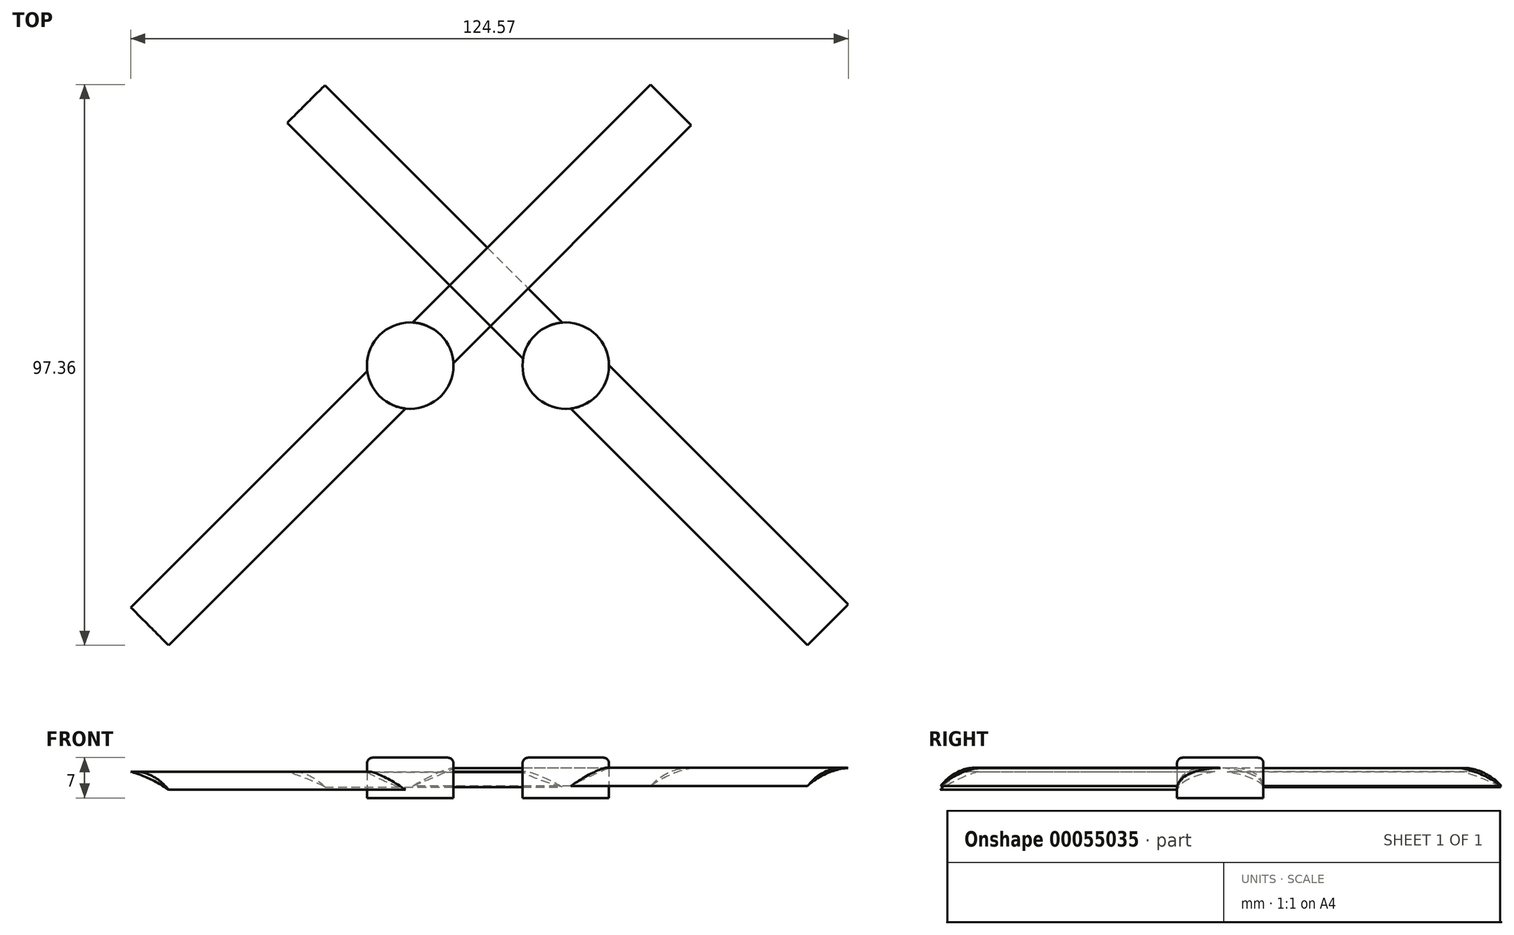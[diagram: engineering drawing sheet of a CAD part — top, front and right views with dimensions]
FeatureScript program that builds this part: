
annotation { "Feature Type Name" : "Feature", "Feature Type Description" : "" }
export const myFeature = defineFeature(function(context is Context, id is Id, definition is map)
    precondition{}
    {
        {
            var Q0;
            Q0=qCreatedBy(makeId("Top.planeOp"),FACE);
            var sketch = newSketch(context, id + "F0", { "sketchPlane" : qUnion([Q0])});
            skCircle(sketch, "E0", {"center": v(0, 0) * mm, "radius": 7.5 * mm});
            skCircle(sketch, "E1", {"center": v(27, 0) * mm, "radius": 7.5 * mm});
            skSolve(sketch);
        }
        {
            var Q0;
            Q0 = qSketchRegion(id + "F0", true);
            extrude(context, id + "F1", {"entities" : qUnion([Q0]), "depth" : 7 * mm});
        }
        {
            var Q0;
            Q0=qCreatedBy(makeId("Front.planeOp"),FACE);
            var sketch = newSketch(context, id + "F2", { "sketchPlane" : qUnion([Q0])});
            skLineSegment(sketch, "E2", {"start": v(-9.64, 5.2) * mm, "end": v(39.2, 5.2) * mm, "construction": true});
            skLineSegment(sketch, "E3", {"start": v(-9.7, 2.1) * mm, "end": v(39.2, 2.1) * mm, "construction": true});
            skLineSegment(sketch, "E4", {"start": v(0, 8.83) * mm, "end": v(0, -3.18) * mm, "construction": true});
            skLineSegment(sketch, "E5", {"start": v(27.35, 8.83) * mm, "end": v(27.35, -3.18) * mm, "construction": true});
            skLineSegment(sketch, "E6", {"start": v(27.35, -3.18) * mm, "end": v(27.76, -3.18) * mm, "construction": true});
            skLineSegment(sketch, "E7.0", {"start": v(-5, 8.83) * mm, "end": v(-5, -3.18) * mm});
            skLineSegment(sketch, "E8.0", {"start": v(22.35, 8.83) * mm, "end": v(22.35, -3.18) * mm});
            skLineSegment(sketch, "E9.0", {"start": v(5, 8.83) * mm, "end": v(5, -3.18) * mm});
            skLineSegment(sketch, "E10.0", {"start": v(32.35, 8.83) * mm, "end": v(32.35, -3.18) * mm});
            skArc(sketch, "E11", {"start": v(5, 5.2) * mm, "mid": v(4.3, 5.22) * mm, "end": v(3.6, 5.2) * mm});
            skArc(sketch, "E12", {"start": v(0.07, 4.1) * mm, "mid": v(0.04, 4.08) * mm, "end": v(0, 4.07) * mm});
            skArc(sketch, "E13", {"start": v(27.42, 4.78) * mm, "mid": v(27.39, 4.8) * mm, "end": v(27.35, 4.8) * mm});
            skPoint(sketch, "E13.startSnap0", {"position": v(32.35, 2.83) * mm});
            skArc(sketch, "E14", {"start": v(27.39, 4.36) * mm, "mid": v(27.37, 4.36) * mm, "end": v(27.35, 4.37) * mm});
            skArc(sketch, "E15", {"start": v(32.35, 5.2) * mm, "mid": v(27.03, 4.67) * mm, "end": v(22.35, 2.1) * mm});
            skArc(sketch, "E16", {"start": v(32.35, 5.2) * mm, "mid": v(27.15, 4.29) * mm, "end": v(22.35, 2.1) * mm});
            skArc(sketch, "E17", {"start": v(5, 2.1) * mm, "mid": v(0.27, 4.51) * mm, "end": v(-5, 5.2) * mm});
            skArc(sketch, "E18", {"start": v(5, 2.1) * mm, "mid": v(0.13, 4.07) * mm, "end": v(-5, 5.2) * mm});
            skArc(sketch, "E19.trimOffspring", {"start": v(0, 4.6) * mm, "mid": v(0, 4.6) * mm, "end": v(-0.02, 4.6) * mm});
            skPoint(sketch, "E20.orphan", {"position": v(32.35, 2.1) * mm});
            skArc(sketch, "E21.trimOffspring", {"start": v(25.37, 5.2) * mm, "mid": v(23.86, 5.29) * mm, "end": v(22.35, 5.2) * mm});
            skSolve(sketch);
        }
        {
            var Q0;
            Q0 = qSketchRegion(id + "F2", true);
            extrude(context, id + "F3", {"entities" : qUnion([Q0]), "operationType" : NewBodyOperationType.ADD, "depth" : 64 * mm});
        }
        {
            var Q0;
            Q0=qCreatedBy(makeId("Front.planeOp"),FACE);
            var sketch = newSketch(context, id + "F4", { "sketchPlane" : qUnion([Q0])});
            skArc(sketch, "E22", {"start": v(4.63, 4.54) * mm, "mid": v(-0.35, 3.92) * mm, "end": v(-4.69, 1.4) * mm});
            skArc(sketch, "E23", {"start": v(4.63, 4.54) * mm, "mid": v(-0.14, 3.3) * mm, "end": v(-4.69, 1.4) * mm});
            skArc(sketch, "E24", {"start": v(31.86, 1.9) * mm, "mid": v(27.46, 4.02) * mm, "end": v(22.6, 4.5) * mm});
            skArc(sketch, "E25", {"start": v(31.86, 1.9) * mm, "mid": v(27.28, 3.38) * mm, "end": v(22.6, 4.5) * mm});
            skSolve(sketch);
        }
        {
            var Q0;
            Q0 = qSketchRegion(id + "F4", true);
            extrude(context, id + "F5", {"entities" : qUnion([Q0]), "operationType" : NewBodyOperationType.ADD, "oppositeDirection" : true, "depth" : 64 * mm});
        }
        {
            var Q0;
            Q0=makeQuery(id+"F1.opExtrude","CAP_EDGE",EDGE,{"disambiguationData":[OSD([sQuery(id+"F0.wireOp",EDGE,"E0")])],"isStart":false});
            var Q1;
            Q1=makeQuery(id+"F1.opExtrude","CAP_EDGE",EDGE,{"disambiguationData":[OSD([sQuery(id+"F0.wireOp",EDGE,"E1")])],"isStart":false});
            fillet(context, id + "F6", {"entities" : qUnion([Q0, Q1]), "radius" : 1 * mm, "tangentPropagation" : true, "allowEdgeOverflow" : false});
        }
        {
            var Q0;
            Q0=makeQuery(id+"F1.opExtrude","SWEPT_BODY",BODY,{"disambiguationData":[OSD([sQuery(id+"F0.wireOp",EDGE,"E0")])]});
            var Q1;
            {var subQ0=sQuery(id+"F0.wireOp",EDGE,"E0");Q1=makeQuery(id+"F6.opFillet","BLEND_EDGE",EDGE,{"blendedFrom":[makeQuery(id+"F1.opExtrude","CAP_EDGE",EDGE,{"disambiguationData":[OSD([subQ0])],"isStart":false}),makeQuery(id+"F1.opExtrude","CAP_FACE",FACE,{"disambiguationData":[OSD([subQ0])],"isStart":false})],"blendedInto":[makeQuery(id+"F1.opExtrude","CAP_FACE",FACE,{"disambiguationData":[OSD([subQ0])],"isStart":false})]});}
            transform(context, id + "F7", {"entities" : qUnion([Q0]), "transformType" : TransformType.ROTATION, "transformAxis" : qUnion([Q1]), "angle" : 45 * degree, "makeCopy" : false});
        }
        {
            var Q0;
            Q0=makeQuery(id+"F1.opExtrude","SWEPT_BODY",BODY,{"disambiguationData":[OSD([sQuery(id+"F0.wireOp",EDGE,"E1")])]});
            var Q1;
            {var subQ0=sQuery(id+"F0.wireOp",EDGE,"E1");Q1=makeQuery(id+"F6.opFillet","BLEND_EDGE",EDGE,{"blendedFrom":[makeQuery(id+"F1.opExtrude","CAP_EDGE",EDGE,{"disambiguationData":[OSD([subQ0])],"isStart":false}),makeQuery(id+"F1.opExtrude","CAP_FACE",FACE,{"disambiguationData":[OSD([subQ0])],"isStart":false})],"blendedInto":[makeQuery(id+"F1.opExtrude","CAP_FACE",FACE,{"disambiguationData":[OSD([subQ0])],"isStart":false})]});}
            transform(context, id + "F8", {"entities" : qUnion([Q0]), "transformType" : TransformType.ROTATION, "transformAxis" : qUnion([Q1]), "angle" : 45 * degree, "makeCopy" : false});
        }
        {
            var Q0;
            Q0=makeQuery(id+"F1.opExtrude","SWEPT_BODY",BODY,{"disambiguationData":[OSD([sQuery(id+"F0.wireOp",EDGE,"E0")])]});
            var Q1;
            {var subQ0=sQuery(id+"F0.wireOp",EDGE,"E0");Q1=makeQuery(id+"F6.opFillet","BLEND_EDGE",EDGE,{"blendedFrom":[makeQuery(id+"F1.opExtrude","CAP_EDGE",EDGE,{"disambiguationData":[OSD([subQ0])],"isStart":false}),makeQuery(id+"F1.opExtrude","CAP_FACE",FACE,{"disambiguationData":[OSD([subQ0])],"isStart":false})],"blendedInto":[makeQuery(id+"F1.opExtrude","CAP_FACE",FACE,{"disambiguationData":[OSD([subQ0])],"isStart":false})]});}
            transform(context, id + "F9", {"entities" : qUnion([Q0]), "transformType" : TransformType.ROTATION, "transformAxis" : qUnion([Q1]), "angle" : 90 * degree, "makeCopy" : false});
        }
    });
